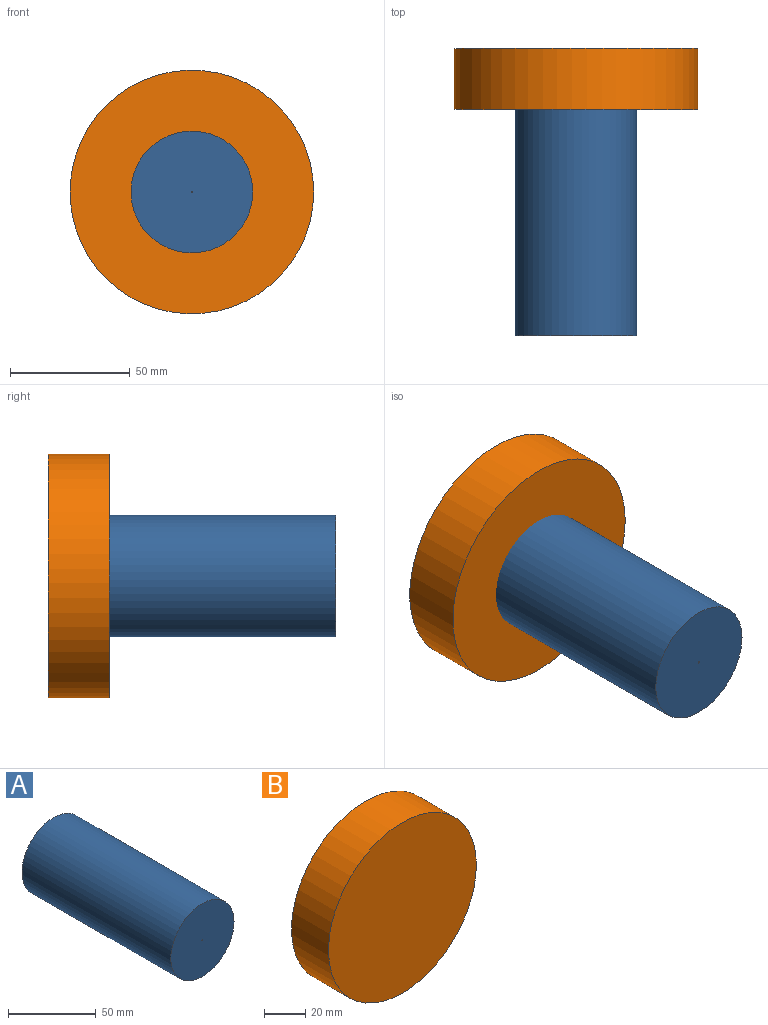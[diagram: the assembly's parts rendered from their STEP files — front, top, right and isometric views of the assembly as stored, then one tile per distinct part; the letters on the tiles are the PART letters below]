
ASSEMBLY  parts=2 mates=1
PART A: 4 faces, bbox 50.8x119.7x50.8 mm
  f0: cylinder r=0.34mm len=119.69mm, axis (0,1,0), area 256.3mm2, adj f2,f3
  f1: cylinder r=25.4mm len=119.69mm, axis (0,1,0), area 19101.2mm2, adj f2,f3
  f2: plane 50.8x50.8mm, normal (0,-1,0), area 2026.5mm2, adj f0,f1
  f3: plane 50.8x50.8mm, normal (0,1,0), area 2026.5mm2, adj f0,f1
PART B: 3 faces, bbox 101.6x25.4x101.6 mm
  f0: cylinder r=50.8mm len=101.6mm, axis (0,1,0), area 8107.3mm2, adj f1,f2
  f1: plane 101.6x101.6mm, normal (0,-1,0), area 8107.3mm2, adj f0
  f2: plane 101.6x101.6mm, normal (0,1,0), area 8107.3mm2, adj f0
PLACE A at identity
PLACE B at identity
MATE cylindrical A.f0 <-> B.f0  axis (0,1,0) through (0,0,0)mm
